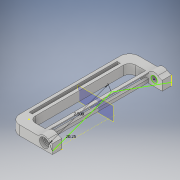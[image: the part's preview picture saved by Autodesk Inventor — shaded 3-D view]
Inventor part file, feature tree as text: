
AUTODESK INVENTOR PART (.ipt)
format: ipt  version: 2018 (Build 220112000, 112)  size: 402,944 bytes
history: native  units: in
note: dims shown in document units (in); Inventor stores cm internally (conversion verified against a paired STEP export)
features: sketch x16, extrude x9, fillet x6, hole x2, plane x1, mirror x1
ambient origin geometry x8: Origin, YZ Plane, XZ Plane, XY Plane, X Axis, Y Axis, Z Axis, Center Point
bodies: Solid1 (feature_tree)
feature tree (35):
  extrude  "Extrusion1"  Depth=0.375in
  sketch  "Sketch2"  dims[d3=0.375in d4=0.5in d5=0.375in d6=0.0in]
  extrude  "Extrusion2"  Depth=0.375in
  fillet  "Fillet1"  Radius=0.375in
  extrude  "Extrusion3"  Depth=0.375in
  extrude  "Extrusion4"  Depth=0.25in
  plane  "Work Plane1"
  mirror  "Mirror1"
  fillet  "Fillet2"  Radius=0.24in
  extrude  "Extrusion5"  Depth=0.375in
  sketch  "Sketch6"  dims[d17=1.0in d18=0.0in d19=0.24in d20=0.0in]
  extrude  "Extrusion6"  Depth=0.24in TaperAngle=0.0deg
  extrude  "Extrusion7"  Depth=0.375in
  fillet  "Fillet3"  Radius=0.25in
  fillet  "Fillet4"  Radius=0.375in
  fillet  "Fillet5"  Radius=0.25in
  fillet  "Fillet6"  Radius=0.125in
  sketch  "Sketch9"  dims[d30=0.125in d31=0.125in]
  extrude  "Extrusion8"  Depth=0.035in
  sketch  "Sketch11"  dims[d35=0.2in]
  sketch  "Sketch12"  dims[d36=0.2in d37=0.75in d38=0.375in d39=0.25in d40=0.5635in d41=0.35in d42=0.0in]
  hole  "Hole1"  [1 undecoded]
  hole  "Hole2"  [1 undecoded]
  sketch  "Sketch14"  dims[d51=3.5in]
  extrude  "Extrusion9"  Depth=0.125in
  sketch  "Sketch16"  dims[d54=2.5in d55=0.1391in]
  sketch  "Sketch1"  dims[d0=1.3in d1=0.375in]
  sketch  "Sketch3"  dims[d7=0.375in d8=0.0in d9=0.375in]
  sketch  "Sketch4"  dims[d10=0.24in d11=0.0in d12=0.25in d13=0.24in d14=0.0in]
  sketch  "Sketch5"  dims[d15=2.0in d16=0.375in]
  sketch  "Sketch7"  dims[d21=0.375in d22=0.0in d23=0.375in d24=0.25in d25=0.375in d26=0.25in d27=0.125in]
  sketch  "Sketch8"  dims[d28=0.035in d29=0.035in]
  sketch  "Sketch10"  dims[d32=4.375in d33=0.0in d34=0.2in]
  sketch  "Sketch13"  dims[d43=0.2in d44=0.75in d45=0.375in d46=0.25in d47=0.5635in d48=0.35in d49=0.0in d50=0.125in]
  sketch  "Sketch15"  dims[d52=0.375in d53=0.0in]
note: 2 required parameter values undecoded (feature->parameter linkage not recoverable at this tier; creation-order binding heuristic only, values carry confidence <= 0.55)
